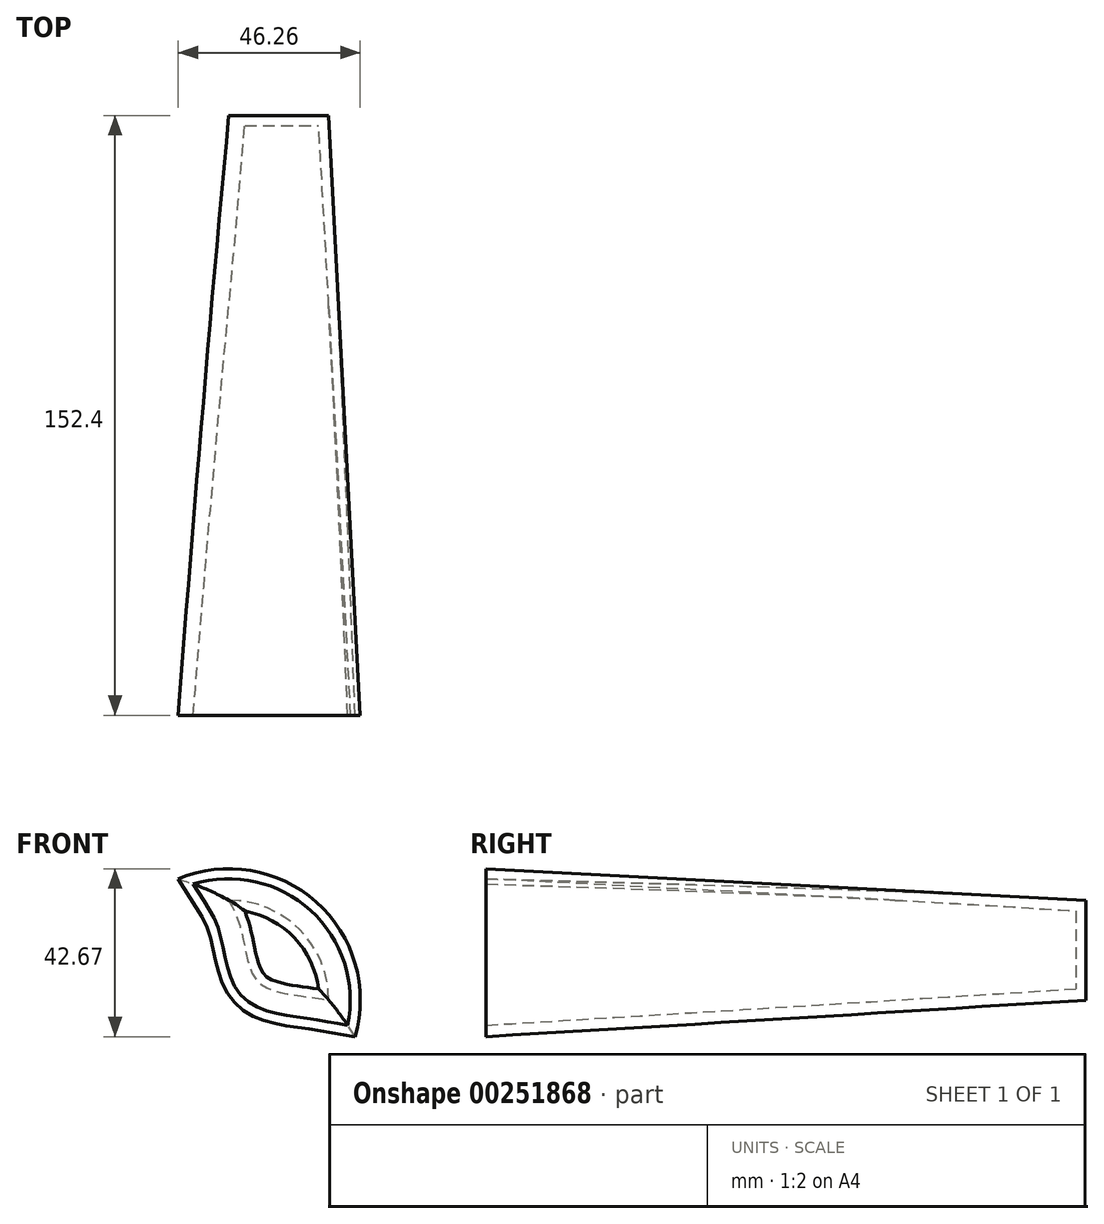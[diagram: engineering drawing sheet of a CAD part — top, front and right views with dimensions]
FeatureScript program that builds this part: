
annotation { "Feature Type Name" : "Feature", "Feature Type Description" : "" }
export const myFeature = defineFeature(function(context is Context, id is Id, definition is map)
    precondition{}
    {
        {
            var Q0;
            Q0=qCreatedBy(makeId("Front.planeOp"),FACE);
            var sketch = newSketch(context, id + "F0", { "sketchPlane" : qUnion([Q0])});
            skPoint(sketch, "E0.middle", {"position": v(0, 0) * mm});
            skPoint(sketch, "E1.visualSharp", {"position": v(-76.2, 50.8) * mm});
            skPoint(sketch, "E2.visualSharp", {"position": v(76.2, 50.8) * mm});
            skArc(sketch, "E2.filletArc", {"start": v(76.2, 25.4) * mm, "mid": v(68.76, 43.36) * mm, "end": v(50.8, 50.8) * mm});
            skPoint(sketch, "E3.visualSharp", {"position": v(-76.2, -50.8) * mm});
            skArc(sketch, "E3.filletArc", {"start": v(-76.2, -25.4) * mm, "mid": v(-68.76, -43.36) * mm, "end": v(-50.8, -50.8) * mm});
            skPoint(sketch, "E4.visualSharp", {"position": v(76.2, -50.8) * mm});
            skFitSpline(sketch, "E5", {"points": [v(-76.2, 25.4) * mm, v(-50.8, 50.8) * mm, v(-36.99, 69.88) * mm, v(-4.62, 57.43) * mm, v(21.34, 64.2) * mm, v(50.8, 50.8) * mm, v(57.61, 30.76) * mm, v(76.2, 25.4) * mm, v(104.56, 7.65) * mm, v(83.93, -25.43) * mm, v(76.2, -25.4) * mm, v(58.68, -30.76) * mm, v(50.8, -50.8) * mm, v(0, -62.77) * mm, v(-50.8, -50.8) * mm, v(-76.2, -25.4) * mm, v(-101.71, 12.27) * mm, v(-76.2, 25.4) * mm]});
            skSolve(sketch);
        }
        {
            var Q0;
            Q0=makeQuery(id+"F0.imprint","IMPRINT",FACE,{"disambiguationData":[TD([[makeQuery(id+"F0.imprint","IMPRINT",EDGE,{"derivedFrom":sQuery(id+"F0.wireOp",EDGE,"E2.filletArc")}),1.0]])]});
            extrude(context, id + "F1", {"entities" : qUnion([Q0]), "depth" : 152.4 * mm, "hasDraft" : true, "draftAngle" : 3 * degree});
        }
        {
            var Q0;
            Q0=makeQuery(id+"F1.opExtrude","CAP_FACE",FACE,{"disambiguationData":[OSD([sQuery(id+"F0.wireOp",EDGE,"E2.filletArc"),sQuery(id+"F0.wireOp",EDGE,"E3.filletArc"),sQuery(id+"F0.wireOp",EDGE,"E5"),sQuery(id+"F0.wireOp",EDGE,"E5")])],"isStart":false});
            shell(context, id + "F2", {"entities" : qUnion([Q0]), "thickness" : 2.54 * mm});
        }
    });
